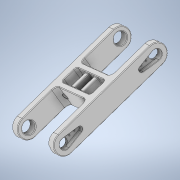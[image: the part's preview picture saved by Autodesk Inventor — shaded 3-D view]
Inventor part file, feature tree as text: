
AUTODESK INVENTOR PART (.ipt)
format: ipt  version: 2020.3 (Build 243373000, 373)  size: 613,376 bytes
history: native  units: mm
features: fillet x14, sketch x9, extrude x8, hole x3, plane x2, chamfer x2
ambient origin geometry x8: Origin, YZ Plane, XZ Plane, XY Plane, X Axis, Y Axis, Z Axis, Center Point
bodies: Solid1 (feature_tree)
feature tree (38):
  extrude  "Extrusion1"  Depth=34.5mm
  sketch  "Sketch2"  dims[d11=20.0mm d12=15.0mm d13=0.0mm d14=3.0mm d15=6.0mm d16=4.0mm d19=6.0mm d20=0.0mm]
  extrude  "Extrusion2"  Depth=15.0mm TaperAngle=0.0deg
  fillet  "Fillet1"  Radius=3.0mm
  fillet  "Fillet2"  Radius=6.0mm
  fillet  "Fillet3"  Radius=4.0mm
  fillet  "Fillet4"  Radius=6.0mm
  sketch  "Sketch5"  dims[d30=35.0mm d31=35.0mm]
  extrude  "Extrusion4"  Depth=35.0mm
  extrude  "Extrusion5"  Depth=12.1mm
  hole  "Hole7"  [1 undecoded]
  extrude  "Extrusion6"  Depth=1.0mm TaperAngle=0.0deg
  extrude  "Extrusion7"  Depth=12.1mm
  hole  "Hole5"  [1 undecoded]
  fillet  "Fillet13"  Radius=0.5mm
  fillet  "Fillet11"  Radius=2.0mm
  fillet  "Fillet9"  Radius=0.2mm
  fillet  "Fillet15"  Radius=3.5mm
  fillet  "Fillet12"  Radius=0.5mm
  hole  "Hole6"  [1 undecoded]
  fillet  "Fillet14"  Radius=0.5mm
  fillet  "Fillet16"  Radius=0.3mm
  fillet  "Fillet17"  Radius=2.0mm
  plane  "Work Plane1"
  plane  "Work Plane2"
  extrude  "Extrusion8"  Depth=2.0mm
  extrude  "Extrusion9"  Depth=2.0mm
  chamfer  "Chamfer1"  Distance=35.0mm
  chamfer  "Chamfer2"  Distance=7.0mm
  fillet  "Fillet20"  Radius=7.0mm
  fillet  "Fillet21"  Radius=0.2mm
  sketch  "Sketch1"  dims[d2=6.0mm d8=34.5mm]
  sketch  "Sketch6"  dims[d53=3.7mm d54=12.1mm]
  sketch  "Sketch12"  dims[d61=4.0mm d62=0.0mm d63=3.5mm d64=0.0mm]
  sketch  "Sketch13"  dims[d68=1.0mm d69=0.0mm d70=1.0mm d71=0.0mm]
  sketch  "Sketch14"  dims[d72=1.0mm d76=12.1mm]
  sketch  "Sketch15"  dims[d89=7.2mm d97=3.5mm]
  sketch  "Sketch16"  dims[d98=4.0mm d99=6.0mm d100=4.0mm d101=2.0mm d102=90.0deg d103=5.0mm d104=20.594885mm d105=0.5mm d107=2.0mm d108=0.2mm d109=3.5mm d110=8.8mm d111=6.0mm d112=4.0mm d113=2.0mm d114=90.0deg d115=5.0mm d116=20.594885mm d117=0.5mm d118=0.5mm d119=0.5mm d120=0.3mm d121=2.0mm d122=2.0mm d123=2.0mm d124=1.0mm d125=6.0mm d126=4.0mm d127=2.0mm d128=90.0deg d129=10.0mm d130=20.594885mm d131=35.0mm d132=7.0mm d133=7.0mm d134=0.0mm d138=0.2mm d139=0.8mm d140=45.0deg d141=1.0mm d142=2.0mm d143=-90.0mm d144=7.0mm d145=0.0mm d146=0.2mm d147=0.8mm d148=45.0deg]
note: 3 required parameter values undecoded (feature->parameter linkage not recoverable at this tier; creation-order binding heuristic only, values carry confidence <= 0.55)
